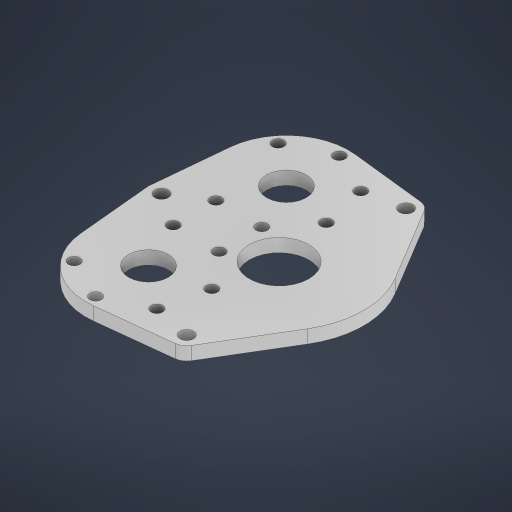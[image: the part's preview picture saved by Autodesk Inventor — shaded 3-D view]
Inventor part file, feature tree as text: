
AUTODESK INVENTOR PART (.ipt)
format: ipt  version: 2024.3 (Build 283343000, 343)  size: 269,824 bytes
history: native  units: in
note: dims shown in document units (in); Inventor stores cm internally (conversion verified against a paired STEP export)
features: extrude x1, sketch x1
ambient origin geometry x8: Origin, YZ Plane, XZ Plane, XY Plane, X Axis, Y Axis, Z Axis, Center Point
bodies: Solid1 (feature_tree)
feature tree (2):
  extrude  "Extrusion1"  Depth=0.25in
  sketch  "Sketch1"  dims[d0=0.5in d1=3.0in d2=0.5in d3=2.36in d4=2.36in d5=0.25in d6=0.1in d8=0.5in d9=0.257in d11=0.25in d12=0.5in d13=0.257in d14=0.25in d15=0.5in d16=0.257in d17=0.25in d18=0.25in d19=1.125in d20=0.75in d21=2.0in d22=0.22in d23=2.7559in d25=360.0deg d27=2.0in d28=2.7559in d30=360.0deg d32=0.25in d33=0.0in]
